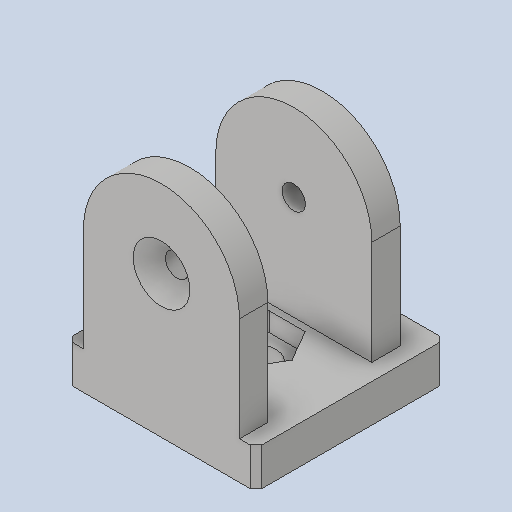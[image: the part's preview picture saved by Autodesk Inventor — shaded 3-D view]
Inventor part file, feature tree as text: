
AUTODESK INVENTOR PART (.ipt)
format: ipt  version: 2023 (Build 270158000, 158)  size: 325,632 bytes
history: native  units: mm
features: other x70, sketch x10, extrude x8, hole x2, chamfer x1
ambient origin geometry x8: Origin, YZ Plane, XZ Plane, XY Plane, X Axis, Y Axis, Z Axis, Center Point
bodies: Solid1 (feature_tree)
feature tree (91):
  extrude  "Extrusion1"  Depth=42.0mm TaperAngle=0.0deg
  extrude  "Extrusion2"  Depth=6.5mm TaperAngle=0.0deg
  extrude  "Extrusion3"  Depth=6.5mm TaperAngle=0.0deg
  hole  "Hole1"  [1 undecoded]
  extrude  "Extrusion4"  TaperAngle=0.0deg  [1 undecoded]
  extrude  "Extrusion5"  TaperAngle=0.0deg  [1 undecoded]
  extrude  "Extrusion6"  TaperAngle=0.0deg  [1 undecoded]
  extrude  "Extrusion7"  TaperAngle=0.0deg  [1 undecoded]
  hole  "Hole2"  [1 undecoded]
  extrude  "Extrusion8"  [1 undecoded]
  other  "GN300Klemmhebel_XY"
  other  "GN300Klemmhebel_YZ"
  other  "GN300Klemmhebel_ZX"
  other  "GN300Klemmhebel_X"
  other  "GN300Klemmhebel_Y"
  other  "GN300Klemmhebel_Z"
  other  "GN300Klemmhebel_Center"
  other  "GUS_4_41_XY"
  other  "GUS_4_41_YZ"
  other  "GUS_4_41_ZX"
  other  "GUS_4_41_X"
  other  "GUS_4_41_Y"
  other  "GUS_4_41_Z"
  other  "GUS_4_41_Center"
  other  "GUS_4_41_L_XY"
  other  "GUS_4_41_L_YZ"
  other  "GUS_4_41_L_ZX"
  other  "GUS_4_41_L_X"
  other  "GUS_4_41_L_Y"
  other  "GUS_4_41_L_Z"
  other  "GUS_4_41_L_Center"
  other  "GUS_4_41_R_XY"
  other  "GUS_4_41_R_YZ"
  other  "GUS_4_41_R_ZX"
  other  "GUS_4_41_R_X"
  other  "GUS_4_41_R_Y"
  other  "GUS_4_41_R_Z"
  other  "GUS_4_41_R_Center"
  other  "p0_XY"
  other  "p0_YZ"
  other  "p0_ZX"
  other  "p0_X"
  other  "p0_Y"
  other  "p0_Z"
  other  "p0_Center"
  other  "p1_XY"
  other  "p1_YZ"
  other  "p1_ZX"
  other  "p1_X"
  other  "p1_Y"
  other  "p1_Z"
  other  "p1_Center"
  other  "p2_XY"
  other  "p2_YZ"
  other  "p2_ZX"
  other  "p2_X"
  other  "p2_Y"
  other  "p2_Z"
  other  "p2_Center"
  other  "p3_XY"
  other  "p3_YZ"
  other  "p3_ZX"
  other  "p3_X"
  other  "p3_Y"
  other  "p3_Z"
  other  "p3_Center"
  other  "p4_XY"
  other  "p4_YZ"
  other  "p4_ZX"
  other  "p4_X"
  other  "p4_Y"
  other  "p4_Z"
  other  "p4_Center"
  other  "ps_XY"
  other  "ps_YZ"
  other  "ps_ZX"
  other  "ps_X"
  other  "ps_Y"
  other  "ps_Z"
  other  "ps_Center"
  chamfer  "Chamfer1"  [1 undecoded]
  sketch  "Skizze_1"  dims[d0=52.0mm d1=0.0mm d2=42.0mm d3=0.0mm]
  sketch  "Skizze_2"  dims[d6=4.92mm d7=6.0mm d8=12.0mm d9=2.0mm d10=16.40943mm d11=39.8mm d12=0.0mm d13=6.5mm d14=0.0mm]
  sketch  "Skizze_3"  dims[d19=6.5mm d20=0.0mm]
  sketch  "Sketch4"  dims[d30=0.0mm d31=0.0mm]
  sketch  "Sketch_1"  dims[d4=42.0mm d5=0.0mm]
  sketch  "Sketch_2"  dims[d15=6.5mm d16=0.0mm d17=6.5mm d18=0.0mm]
  sketch  "Sketch_3"  dims[d21=8.5mm d22=6.0mm d23=4.0mm d24=2.0mm d25=90.0deg d26=8.0mm d27=0.0mm d28=4.0mm d29=0.0mm]
  sketch  "Sketch_4"  dims[d32=0.0mm d33=0.0mm]
  sketch  "Sketch9"  dims[d36=0.0mm d37=0.0mm d38=1.25mm d39=2.0mm d40=45.0deg]
  sketch  "Sketch_5"  dims[d34=0.0mm d35=0.0mm]
note: 8 required parameter values undecoded (feature->parameter linkage not recoverable at this tier; creation-order binding heuristic only, values carry confidence <= 0.55)
